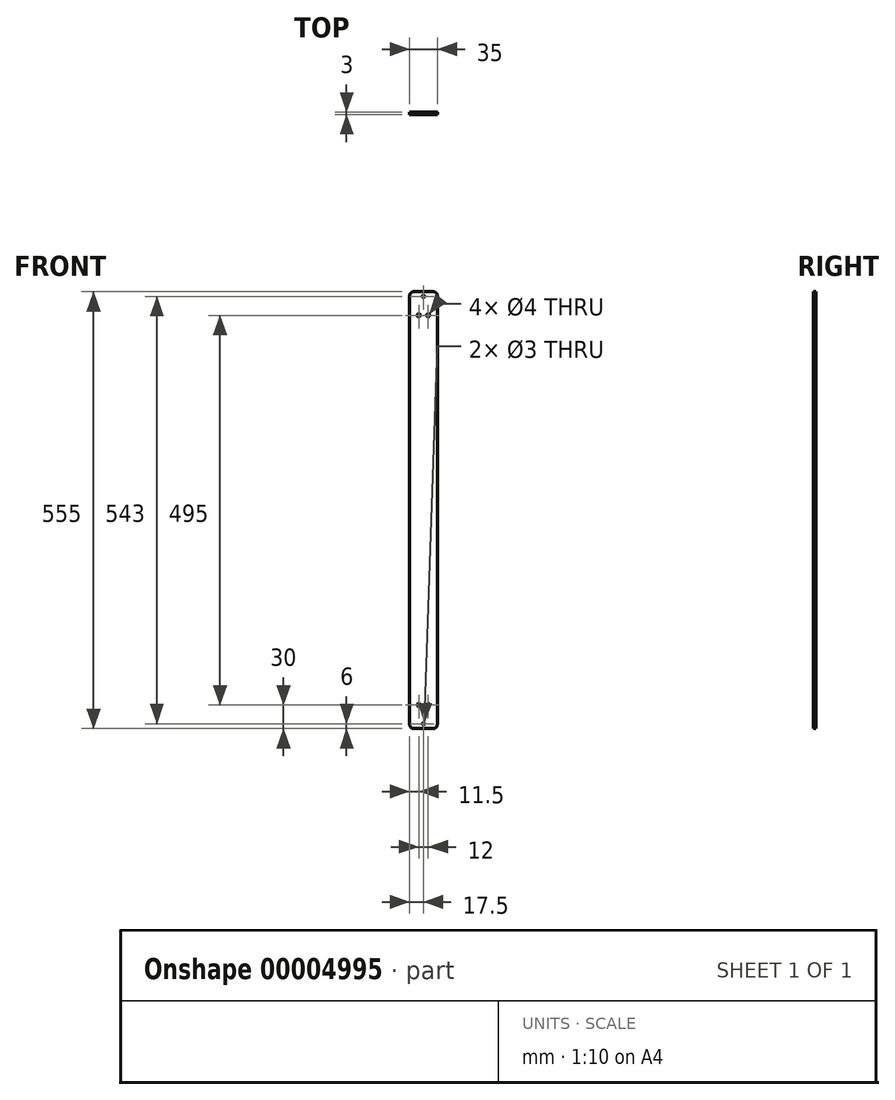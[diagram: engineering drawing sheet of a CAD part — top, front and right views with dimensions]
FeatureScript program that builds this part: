
annotation { "Feature Type Name" : "Feature", "Feature Type Description" : "" }
export const myFeature = defineFeature(function(context is Context, id is Id, definition is map)
    precondition{}
    {
        {
            var Q0;
            Q0=qCreatedBy(makeId("Front.planeOp"),FACE);
            var sketch = newSketch(context, id + "F0", { "sketchPlane" : qUnion([Q0])});
            skLineSegment(sketch, "E0.rect.bottom", {"start": v(17.5, 277.5) * mm, "end": v(-17.5, 277.5) * mm});
            skLineSegment(sketch, "E0.rect.top", {"start": v(17.5, -277.5) * mm, "end": v(-17.5, -277.5) * mm});
            skLineSegment(sketch, "E0.rect.left", {"start": v(17.5, 277.5) * mm, "end": v(17.5, -277.5) * mm});
            skLineSegment(sketch, "E0.rect.right", {"start": v(-17.5, 277.5) * mm, "end": v(-17.5, -277.5) * mm});
            skPoint(sketch, "E0.rect.middle", {"position": v(0, 0) * mm});
            skLineSegment(sketch, "E1", {"start": v(0, 277.5) * mm, "end": v(0, -277.5) * mm, "construction": true});
            skLineSegment(sketch, "E2", {"start": v(0, 0) * mm, "end": v(17.5, 0) * mm, "construction": true});
            skCircle(sketch, "E3", {"center": v(0, 271.5) * mm, "radius": 1.5 * mm});
            skCircle(sketch, "E4.0.MirrorC", {"center": v(0, -271.5) * mm, "radius": 1.5 * mm});
            skSolve(sketch);
        }
        {
            var Q0;
            Q0=qSketchRegion(id+"F0",true);
            extrude(context, id + "F1", {"entities" : qUnion([Q0]), "depth" : 3 * mm});
        }
        {
            var Q0;
            Q0=makeQuery(id+"F1.opExtrude","SWEPT_EDGE",EDGE,{"disambiguationData":[OSD([sQuery(id+"F0.wireOp",EDGE,"E0.rect.bottom"),sQuery(id+"F0.wireOp",EDGE,"E0.rect.left")])]});
            var Q1;
            Q1=makeQuery(id+"F1.opExtrude","SWEPT_EDGE",EDGE,{"disambiguationData":[OSD([sQuery(id+"F0.wireOp",EDGE,"E0.rect.bottom"),sQuery(id+"F0.wireOp",EDGE,"E0.rect.right")])]});
            var Q2;
            Q2=makeQuery(id+"F1.opExtrude","SWEPT_EDGE",EDGE,{"disambiguationData":[OSD([sQuery(id+"F0.wireOp",EDGE,"E0.rect.top"),sQuery(id+"F0.wireOp",EDGE,"E0.rect.left")])]});
            var Q3;
            Q3=makeQuery(id+"F1.opExtrude","SWEPT_EDGE",EDGE,{"disambiguationData":[OSD([sQuery(id+"F0.wireOp",EDGE,"E0.rect.top"),sQuery(id+"F0.wireOp",EDGE,"E0.rect.right")])]});
            fillet(context, id + "F2", {"entities" : qUnion([Q0, Q1, Q2, Q3]), "radius" : 5 * mm, "tangentPropagation" : true, "allowEdgeOverflow" : false});
        }
        {
            var Q0;
            Q0=makeQuery(id+"F1.opExtrude","CAP_FACE",FACE,{"disambiguationData":[OSD([sQuery(id+"F0.wireOp",EDGE,"E0.rect.bottom"),sQuery(id+"F0.wireOp",EDGE,"E0.rect.top"),sQuery(id+"F0.wireOp",EDGE,"E0.rect.left"),sQuery(id+"F0.wireOp",EDGE,"E0.rect.right"),sQuery(id+"F0.wireOp",EDGE,"E3"),sQuery(id+"F0.wireOp",EDGE,"E4.0.MirrorC")])],"isStart":false});
            var sketch = newSketch(context, id + "F3", { "sketchPlane" : qUnion([Q0])});
            skLineSegment(sketch, "E5", {"start": v(-17.5, 0) * mm, "end": v(17.5, 0) * mm, "construction": true});
            skLineSegment(sketch, "E6", {"start": v(-17.5, -247.5) * mm, "end": v(17.5, -247.5) * mm, "construction": true});
            skCircle(sketch, "E7", {"center": v(6, -247.5) * mm, "radius": 2 * mm});
            skCircle(sketch, "E8", {"center": v(-6, -247.5) * mm, "radius": 2 * mm});
            skCircle(sketch, "E9.0.MirrorC", {"center": v(6, 247.5) * mm, "radius": 2 * mm});
            skCircle(sketch, "E9.1.MirrorC", {"center": v(-6, 247.5) * mm, "radius": 2 * mm});
            skSolve(sketch);
        }
        {
            var Q0;
            Q0 = qSketchRegion(id + "F3", true);
            extrude(context, id + "F4", {"entities" : qUnion([Q0]), "operationType" : NewBodyOperationType.REMOVE, "endBound" : BoundingType.THROUGH_ALL, "oppositeDirection" : true, "depth" : 25 * mm});
        }
    });
